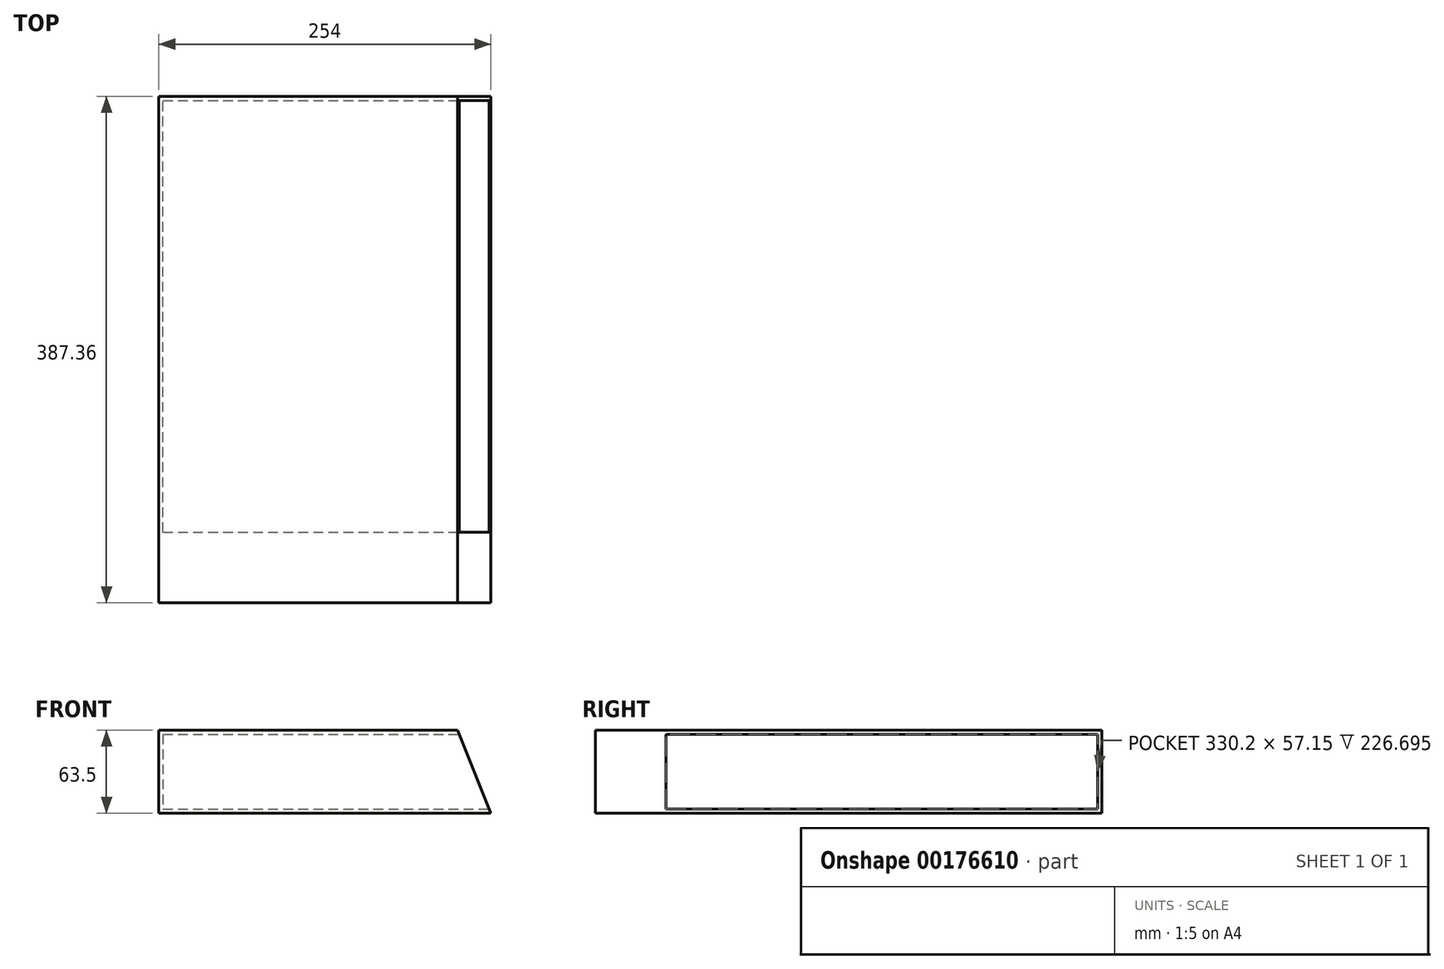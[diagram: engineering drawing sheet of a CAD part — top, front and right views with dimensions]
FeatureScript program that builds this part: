
annotation { "Feature Type Name" : "Feature", "Feature Type Description" : "" }
export const myFeature = defineFeature(function(context is Context, id is Id, definition is map)
    precondition{}
    {
        {
            var Q0;
            Q0=qCreatedBy(makeId("Front.planeOp"),FACE);
            var sketch = newSketch(context, id + "F0", { "sketchPlane" : qUnion([Q0])});
            skLineSegment(sketch, "E0", {"start": v(-134.88, 0) * mm, "end": v(119.12, 0) * mm});
            skLineSegment(sketch, "E1", {"start": v(-134.88, 0) * mm, "end": v(-134.88, 63.5) * mm});
            skLineSegment(sketch, "E2", {"start": v(-134.88, 63.5) * mm, "end": v(93.72, 63.5) * mm});
            skLineSegment(sketch, "E3", {"start": v(93.72, 63.5) * mm, "end": v(119.12, 0) * mm, "construction": true});
            skLineSegment(sketch, "E4", {"start": v(-131.7, 60.33) * mm, "end": v(94.99, 60.33) * mm});
            skLineSegment(sketch, "E5", {"start": v(-131.7, 3.18) * mm, "end": v(117.85, 3.18) * mm});
            skLineSegment(sketch, "E6", {"start": v(-131.7, 60.33) * mm, "end": v(-131.7, 3.18) * mm});
            skLineSegment(sketch, "E7", {"start": v(93.72, 63.5) * mm, "end": v(94.99, 60.33) * mm});
            skLineSegment(sketch, "E8", {"start": v(117.85, 3.17) * mm, "end": v(119.12, 0) * mm});
            skLineSegment(sketch, "E9", {"start": v(94.99, 60.33) * mm, "end": v(117.85, 3.18) * mm});
            skSolve(sketch);
        }
        {
            var Q0;
            Q0=makeQuery(id+"F0.imprint","IMPRINT",FACE,{"disambiguationData":[TD([[makeQuery(id+"F0.imprint","IMPRINT",EDGE,{"derivedFrom":sQuery(id+"F0.wireOp",EDGE,"E0")}),1.0]])]});
            extrude(context, id + "F1", {"entities" : qUnion([Q0]), "depth" : 330.2 * mm});
        }
        {
            var Q0;
            Q0=makeQuery(id+"F0.imprint","IMPRINT",FACE,{"disambiguationData":[TD([[makeQuery(id+"F0.imprint","IMPRINT",EDGE,{"derivedFrom":sQuery(id+"F0.wireOp",EDGE,"E4")}),-1.0]])]});
            var Q1;
            Q1=makeQuery(id+"F0.imprint","IMPRINT",FACE,{"disambiguationData":[TD([[makeQuery(id+"F0.imprint","IMPRINT",EDGE,{"derivedFrom":sQuery(id+"F0.wireOp",EDGE,"E0")}),1.0]])]});
            extrude(context, id + "F2", {"entities" : qUnion([Q0, Q1]), "operationType" : NewBodyOperationType.ADD, "oppositeDirection" : true, "depth" : 3.17 * mm});
        }
        {
            var Q0;
            Q0=makeQuery(id+"F1.opExtrude","CAP_FACE",FACE,{"disambiguationData":[OSD([sQuery(id+"F0.wireOp",EDGE,"E0"),sQuery(id+"F0.wireOp",EDGE,"E1"),sQuery(id+"F0.wireOp",EDGE,"E2"),sQuery(id+"F0.wireOp",EDGE,"E4"),sQuery(id+"F0.wireOp",EDGE,"E5"),sQuery(id+"F0.wireOp",EDGE,"E6"),sQuery(id+"F0.wireOp",EDGE,"E7"),sQuery(id+"F0.wireOp",EDGE,"E8")])],"isStart":false});
            var sketch = newSketch(context, id + "F3", { "sketchPlane" : qUnion([Q0])});
            skLineSegment(sketch, "E10", {"start": v(93.72, 63.5) * mm, "end": v(119.12, 0) * mm});
            skLineSegment(sketch, "E11", {"start": v(119.12, 0) * mm, "end": v(-134.88, 0) * mm});
            skLineSegment(sketch, "E12", {"start": v(-134.88, 0) * mm, "end": v(-134.88, 63.5) * mm});
            skLineSegment(sketch, "E13", {"start": v(-134.88, 63.5) * mm, "end": v(93.72, 63.5) * mm});
            skSolve(sketch);
        }
        {
            var Q0;
            {var subQ1=makeQuery(id+"F1.opExtrude","CAP_EDGE",EDGE,{"disambiguationData":[OSD([sQuery(id+"F0.wireOp",EDGE,"E4")])],"isStart":false});Q0=makeQuery(id+"F3.imprint","IMPRINT",FACE,{"disambiguationData":[TD([[makeQuery(id+"F3.imprint","IMPRINT",EDGE,{"derivedFrom":subQ1}),-1.0]])]});}
            var Q1;
            {var subQ0=sQuery(id+"F3.wireOp",EDGE,"E11");Q1=makeQuery(id+"F3.imprint","IMPRINT",FACE,{"disambiguationData":[TD([[makeQuery(id+"F3.imprint","IMPRINT",EDGE,{"derivedFrom":subQ0}),1.0]])]});}
            extrude(context, id + "F4", {"entities" : qUnion([Q0, Q1]), "operationType" : NewBodyOperationType.ADD, "depth" : 53.97 * mm});
        }
    });
